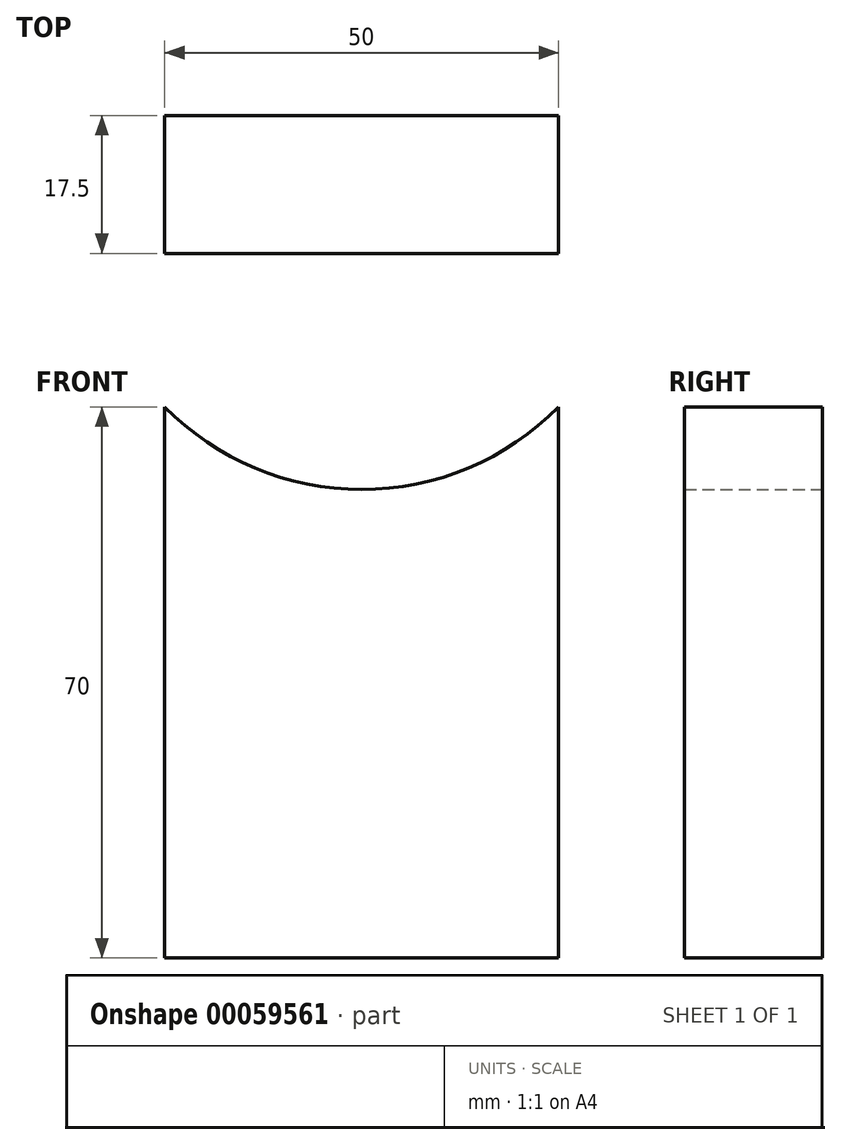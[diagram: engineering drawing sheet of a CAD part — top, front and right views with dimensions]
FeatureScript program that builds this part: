
annotation { "Feature Type Name" : "Feature", "Feature Type Description" : "" }
export const myFeature = defineFeature(function(context is Context, id is Id, definition is map)
    precondition{}
    {
        {
            var Q0;
            Q0=qCreatedBy(makeId("Front.planeOp"),FACE);
            var sketch = newSketch(context, id + "F0", { "sketchPlane" : qUnion([Q0])});
            skLineSegment(sketch, "E0.rect.top", {"start": v(-25, -35) * mm, "end": v(25, -35) * mm});
            skLineSegment(sketch, "E0.rect.left", {"start": v(-25, 35) * mm, "end": v(-25, -35) * mm});
            skLineSegment(sketch, "E0.rect.right", {"start": v(25, 35) * mm, "end": v(25, -35) * mm});
            skPoint(sketch, "E0.rect.middle", {"position": v(0, 0) * mm});
            skArc(sketch, "E1", {"start": v(-25, 35) * mm, "mid": v(0, 24.5) * mm, "end": v(25, 35) * mm});
            skSolve(sketch);
        }
        {
            var Q0;
            Q0=makeQuery(id+"F0.imprint","IMPRINT",FACE,{"disambiguationData":[TD([[makeQuery(id+"F0.imprint","IMPRINT",EDGE,{"derivedFrom":sQuery(id+"F0.wireOp",EDGE,"E0.rect.top")}),1.0]])]});
            extrude(context, id + "F1", {"entities" : qUnion([Q0]), "depth" : 17.5 * mm});
        }
    });
